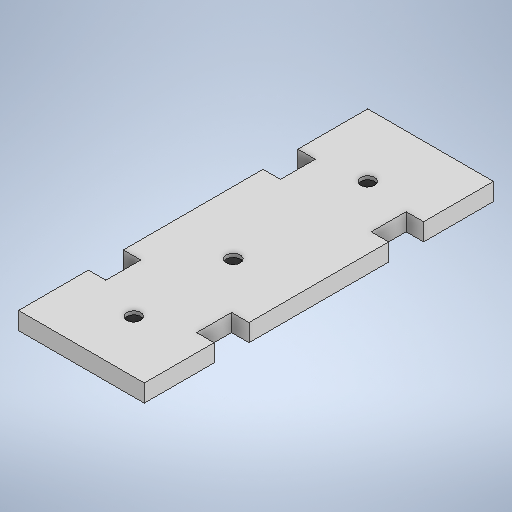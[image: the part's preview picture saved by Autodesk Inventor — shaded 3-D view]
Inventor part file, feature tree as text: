
AUTODESK INVENTOR PART (.ipt)
format: ipt  version: 2025.2 (Build 292293000, 293)  size: 272,896 bytes
history: native  units: mm
features: extrude x2, sketch x2
ambient origin geometry x8: Origin, YZ Plane, XZ Plane, XY Plane, X Axis, Y Axis, Z Axis, Center Point
bodies: Solid1 (feature_tree)
feature tree (4):
  extrude  "Extrusion1"  Depth=100.0mm
  extrude  "Extrusion2"  Depth=20.0mm
  sketch  "Sketch2"  dims[d0=36.0mm d1=100.0mm]
  sketch  "Sketch3"  dims[d2=20.0mm d3=20.0mm d4=10.0mm d5=5.0mm d6=10.0mm d7=5.0mm d8=5.0mm d9=15.0mm d11=28.5mm d12=10.1mm d13=38.5mm d14=10.1mm d15=5.0mm d16=0.0mm d18=4.0mm d19=4.0mm d20=4.0mm d21=1.0mm d22=0.0mm]
